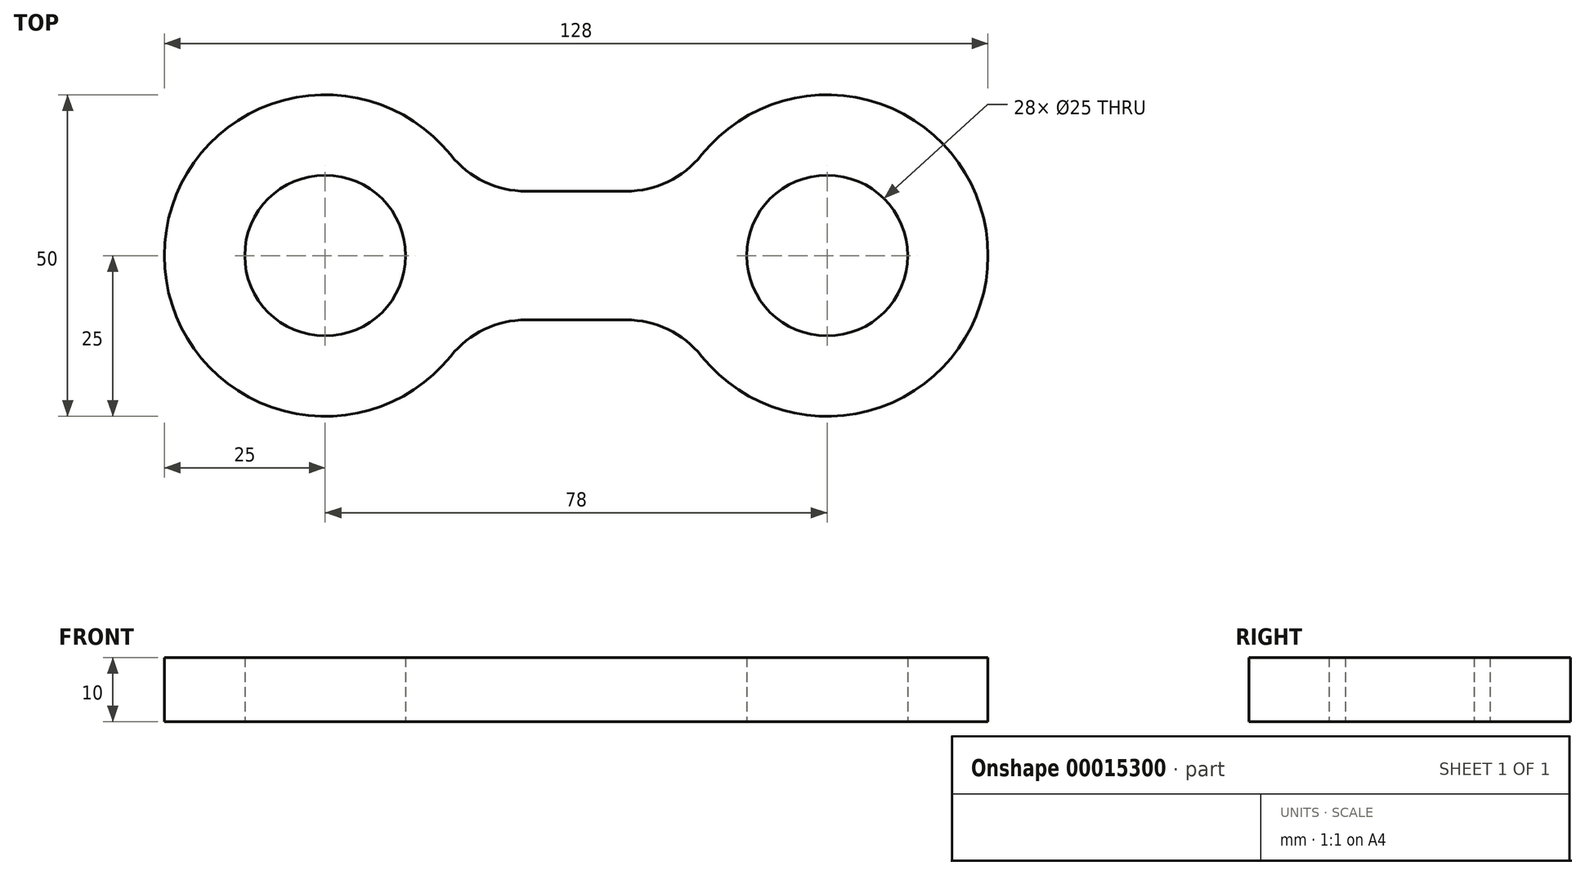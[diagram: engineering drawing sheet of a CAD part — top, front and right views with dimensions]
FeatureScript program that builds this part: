
annotation { "Feature Type Name" : "Feature", "Feature Type Description" : "" }
export const myFeature = defineFeature(function(context is Context, id is Id, definition is map)
    precondition{}
    {
        {
            var Q0;
            Q0=qCreatedBy(makeId("Top.planeOp"),FACE);
            var sketch = newSketch(context, id + "F0", { "sketchPlane" : qUnion([Q0])});
            skArc(sketch, "E0", {"start": v(19.52, 15.63) * mm, "mid": v(-25, 0) * mm, "end": v(19.52, -15.63) * mm});
            skArc(sketch, "E1", {"start": v(58.48, -15.62) * mm, "mid": v(103, 0) * mm, "end": v(58.48, 15.62) * mm});
            skLineSegment(sketch, "E2", {"start": v(31.22, 10) * mm, "end": v(46.78, 10) * mm});
            skLineSegment(sketch, "E3", {"start": v(0, 0) * mm, "end": v(78, 0) * mm, "construction": true});
            skLineSegment(sketch, "E4.MirrorCS", {"start": v(31.22, -10) * mm, "end": v(46.78, -10) * mm});
            skPoint(sketch, "E5.visualSharp", {"position": v(22.91, 10) * mm});
            skArc(sketch, "E5.filletArc", {"start": v(19.52, 15.62) * mm, "mid": v(24.73, 11.48) * mm, "end": v(31.22, 10) * mm});
            skPoint(sketch, "E6.visualSharp", {"position": v(22.91, -10) * mm});
            skArc(sketch, "E6.filletArc", {"start": v(31.22, -10) * mm, "mid": v(24.73, -11.48) * mm, "end": v(19.52, -15.62) * mm});
            skPoint(sketch, "E7.visualSharp", {"position": v(55.09, -10) * mm});
            skArc(sketch, "E7.filletArc", {"start": v(58.48, -15.62) * mm, "mid": v(53.27, -11.48) * mm, "end": v(46.78, -10) * mm});
            skPoint(sketch, "E8.visualSharp", {"position": v(55.09, 10) * mm});
            skArc(sketch, "E8.filletArc", {"start": v(46.78, 10) * mm, "mid": v(53.27, 11.48) * mm, "end": v(58.48, 15.62) * mm});
            skCircle(sketch, "E9", {"center": v(0, 0) * mm, "radius": 12.5 * mm});
            skCircle(sketch, "E10", {"center": v(78, 0) * mm, "radius": 12.5 * mm});
            skSolve(sketch);
        }
        {
            var Q0;
            Q0=qSketchRegion(id+"F0",true);
            extrude(context, id + "F1", {"entities" : qUnion([Q0]), "depth" : 10 * mm});
        }
    });
